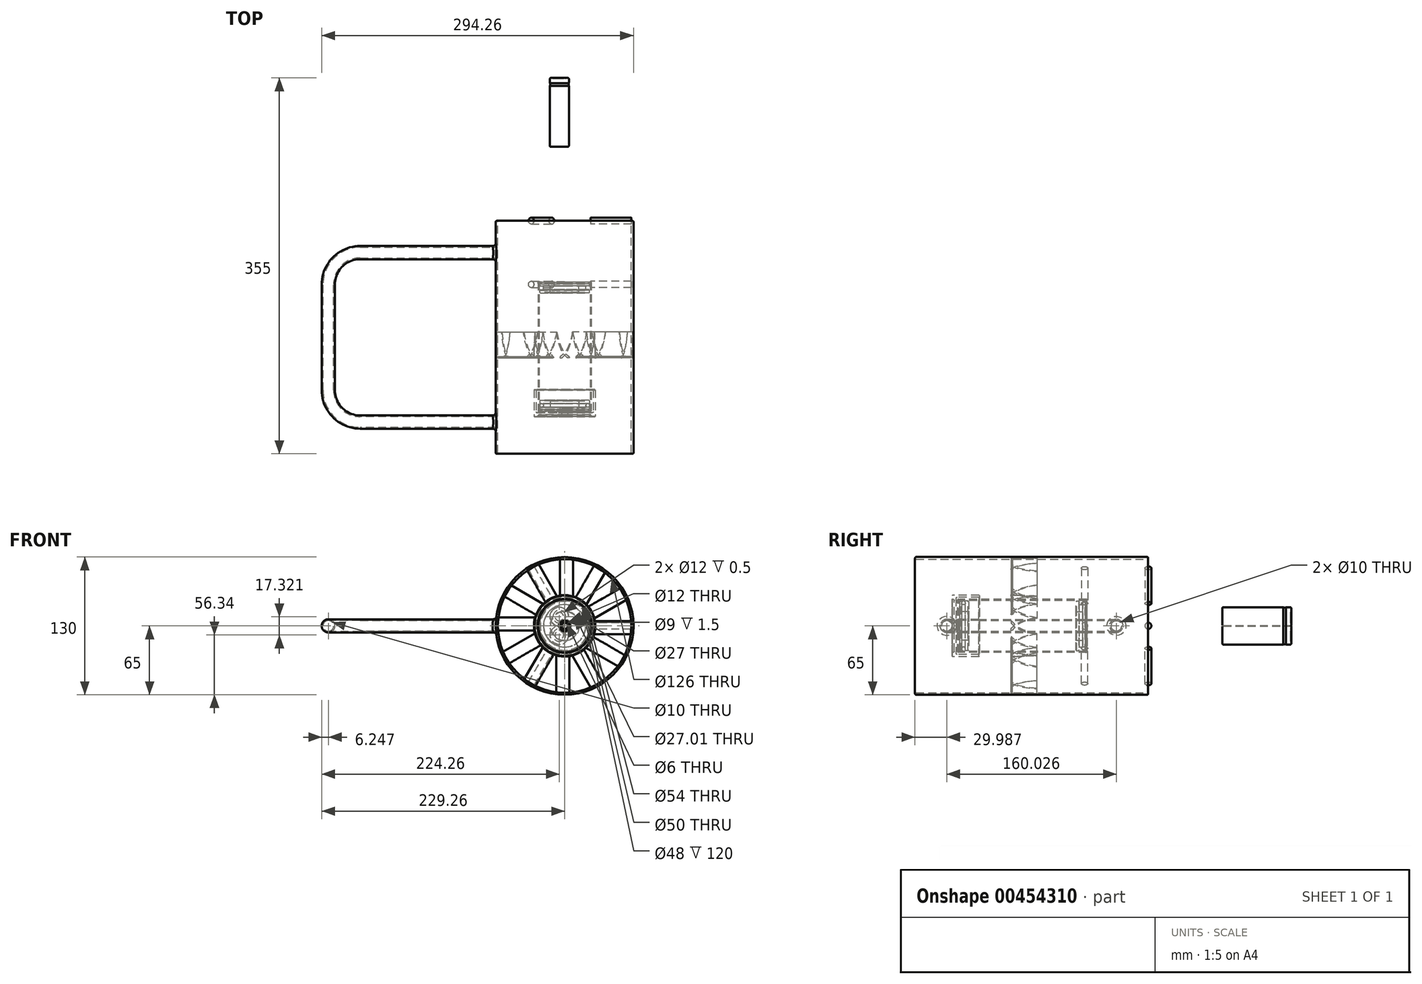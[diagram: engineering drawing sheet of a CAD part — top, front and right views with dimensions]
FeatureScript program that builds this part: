
annotation { "Feature Type Name" : "Feature", "Feature Type Description" : "" }
export const myFeature = defineFeature(function(context is Context, id is Id, definition is map)
    precondition{}
    {
        {
            var Q0;
            Q0=qCreatedBy(makeId("Right.planeOp"),FACE);
            var sketch = newSketch(context, id + "F0", { "sketchPlane" : qUnion([Q0])});
            skLineSegment(sketch, "E0", {"start": v(0, 0) * mm, "end": v(0, 5.8) * mm});
            skLineSegment(sketch, "E1", {"start": v(0.2, 6) * mm, "end": v(2, 6) * mm});
            skLineSegment(sketch, "E2", {"start": v(2, 6) * mm, "end": v(2, 4.31) * mm});
            skLineSegment(sketch, "E3", {"start": v(1.68, 3.67) * mm, "end": v(0.77, 3) * mm});
            skLineSegment(sketch, "E4", {"start": v(0.77, 3) * mm, "end": v(0.46, 3.46) * mm});
            skLineSegment(sketch, "E5", {"start": v(0.46, 3.46) * mm, "end": v(0.97, 4.13) * mm});
            skLineSegment(sketch, "E6", {"start": v(0.81, 4.53) * mm, "end": v(0, 4.66) * mm});
            skArc(sketch, "E7.filletArc", {"start": v(0.97, 4.13) * mm, "mid": v(1, 4.38) * mm, "end": v(0.81, 4.53) * mm});
            skPoint(sketch, "E8.visualSharp", {"position": v(0, 6) * mm});
            skArc(sketch, "E8.filletArc", {"start": v(0.2, 6) * mm, "mid": v(0.06, 5.94) * mm, "end": v(0, 5.8) * mm});
            skPoint(sketch, "E9.visualSharp", {"position": v(2, 3.9) * mm});
            skArc(sketch, "E9.filletArc", {"start": v(1.68, 3.67) * mm, "mid": v(1.91, 3.95) * mm, "end": v(2, 4.31) * mm});
            skLineSegment(sketch, "E10", {"start": v(-2.35, 0) * mm, "end": v(5.53, 0) * mm, "construction": true});
            skSolve(sketch);
        }
        {
            var Q0;
            Q0=qSketchRegion(id+"F0",true);
            var Q1;
            Q1=sQuery(id+"F0.wireOp",EDGE,"E10");
            revolve(context, id + "F1", {"entities" : qUnion([Q0]), "axis" : qUnion([Q1]), "revolveType" : RevolveType.FULL});
        }
        {
            var Q0;
            Q0=makeQuery(id+"F1.opRevolve","SWEPT_BODY",BODY,{"disambiguationData":[OSD([sQuery(id+"F0.wireOp",EDGE,"E0"),sQuery(id+"F0.wireOp",EDGE,"E1"),sQuery(id+"F0.wireOp",EDGE,"E2"),sQuery(id+"F0.wireOp",EDGE,"E3"),sQuery(id+"F0.wireOp",EDGE,"E4"),sQuery(id+"F0.wireOp",EDGE,"E5"),sQuery(id+"F0.wireOp",EDGE,"E6"),sQuery(id+"F0.wireOp",EDGE,"E7.filletArc"),sQuery(id+"F0.wireOp",EDGE,"E8.filletArc"),sQuery(id+"F0.wireOp",EDGE,"E9.filletArc")])]});
            var Q1;
            Q1=makeQuery(id+"F1.opRevolve","SWEPT_FACE",FACE,{"disambiguationData":[OSD([sQuery(id+"F0.wireOp",EDGE,"E1")])]});
            var Q2;
            Q2=qCreatedBy(makeId("Top.planeOp"),FACE);
            transform(context, id + "F2", {"entities" : qUnion([Q0]), "transformType" : TransformType.TRANSLATION_DISTANCE, "transformDirection" : qUnion([Q1, Q2]), "distance" : 50 * mm, "makeCopy" : false});
        }
        {
            var Q0;
            Q0=qCreatedBy(makeId("Right.planeOp"),FACE);
            var sketch = newSketch(context, id + "F3", { "sketchPlane" : qUnion([Q0])});
            skLineSegment(sketch, "E11", {"start": v(0, 0) * mm, "end": v(0, 25) * mm});
            skLineSegment(sketch, "E12", {"start": v(0, 25) * mm, "end": v(2, 25) * mm});
            skLineSegment(sketch, "E13", {"start": v(2, 25) * mm, "end": v(2, 23.5) * mm});
            skLineSegment(sketch, "E14", {"start": v(2, 23.5) * mm, "end": v(4, 23.5) * mm});
            skLineSegment(sketch, "E15", {"start": v(4, 23.5) * mm, "end": v(4, 20) * mm});
            skLineSegment(sketch, "E16", {"start": v(4, 20) * mm, "end": v(7.5, 20) * mm});
            skLineSegment(sketch, "E17", {"start": v(7.5, 20) * mm, "end": v(7.5, 23.5) * mm});
            skLineSegment(sketch, "E18", {"start": v(7.5, 23.5) * mm, "end": v(10.5, 23.5) * mm});
            skLineSegment(sketch, "E19", {"start": v(10.5, 23.5) * mm, "end": v(10.5, 13.5) * mm});
            skLineSegment(sketch, "E20", {"start": v(10.5, 13.5) * mm, "end": v(4, 13.5) * mm});
            skLineSegment(sketch, "E21", {"start": v(4, 13.5) * mm, "end": v(4, 4.5) * mm});
            skLineSegment(sketch, "E22", {"start": v(4, 4.5) * mm, "end": v(2.5, 4.5) * mm});
            skLineSegment(sketch, "E23", {"start": v(2.5, 4.5) * mm, "end": v(2.5, 6) * mm});
            skLineSegment(sketch, "E24", {"start": v(2.5, 6) * mm, "end": v(0, 6) * mm});
            skLineSegment(sketch, "E25", {"start": v(-5.31, 0) * mm, "end": v(25.38, 0) * mm, "construction": true});
            skSolve(sketch);
        }
        {
            var Q0;
            Q0=qSketchRegion(id+"F3",true);
            var Q1;
            Q1=sQuery(id+"F3.wireOp",EDGE,"E25");
            revolve(context, id + "F4", {"entities" : qUnion([Q0]), "axis" : qUnion([Q1]), "revolveType" : RevolveType.FULL});
        }
        {
            var Q0;
            Q0=makeQuery(id+"F4.opRevolve","SWEPT_EDGE",EDGE,{"disambiguationData":[OSD([sQuery(id+"F3.wireOp",EDGE,"E11"),sQuery(id+"F3.wireOp",EDGE,"E24")])]});
            chamfer(context, id + "F5", {"entities" : qUnion([Q0]), "chamferType" : ChamferType.OFFSET_ANGLE, "width" : .5 * mm, "oppositeDirection" : false, "angle" : 30 * degree, "tangentPropagation" : true});
        }
        {
            var Q0;
            Q0=makeQuery(id+"F4.opRevolve","SWEPT_EDGE",EDGE,{"disambiguationData":[OSD([sQuery(id+"F3.wireOp",EDGE,"E23"),sQuery(id+"F3.wireOp",EDGE,"E24")])]});
            var Q1;
            Q1=makeQuery(id+"F4.opRevolve","SWEPT_EDGE",EDGE,{"disambiguationData":[OSD([sQuery(id+"F3.wireOp",EDGE,"E17"),sQuery(id+"F3.wireOp",EDGE,"E18")])]});
            var Q2;
            Q2=makeQuery(id+"F4.opRevolve","SWEPT_EDGE",EDGE,{"disambiguationData":[OSD([sQuery(id+"F3.wireOp",EDGE,"E15"),sQuery(id+"F3.wireOp",EDGE,"E16")])]});
            var Q3;
            Q3=makeQuery(id+"F4.opRevolve","SWEPT_EDGE",EDGE,{"disambiguationData":[OSD([sQuery(id+"F3.wireOp",EDGE,"E20"),sQuery(id+"F3.wireOp",EDGE,"E21")])]});
            fillet(context, id + "F6", {"entities" : qUnion([Q0, Q1, Q2, Q3]), "radius" : .3 * mm, "tangentPropagation" : true, "allowEdgeOverflow" : false});
        }
        {
            var Q0;
            Q0=makeQuery(id+"F4.opRevolve","SWEPT_EDGE",EDGE,{"disambiguationData":[OSD([sQuery(id+"F3.wireOp",EDGE,"E11"),sQuery(id+"F3.wireOp",EDGE,"E12")])]});
            var Q1;
            Q1=makeQuery(id+"F4.opRevolve","SWEPT_EDGE",EDGE,{"disambiguationData":[OSD([sQuery(id+"F3.wireOp",EDGE,"E12"),sQuery(id+"F3.wireOp",EDGE,"E13")])]});
            var Q2;
            Q2=makeQuery(id+"F4.opRevolve","SWEPT_EDGE",EDGE,{"disambiguationData":[OSD([sQuery(id+"F3.wireOp",EDGE,"E14"),sQuery(id+"F3.wireOp",EDGE,"E15")])]});
            var Q3;
            Q3=makeQuery(id+"F4.opRevolve","SWEPT_EDGE",EDGE,{"disambiguationData":[OSD([sQuery(id+"F3.wireOp",EDGE,"E17"),sQuery(id+"F3.wireOp",EDGE,"E18")])]});
            var Q4;
            Q4=makeQuery(id+"F4.opRevolve","SWEPT_EDGE",EDGE,{"disambiguationData":[OSD([sQuery(id+"F3.wireOp",EDGE,"E18"),sQuery(id+"F3.wireOp",EDGE,"E19")])]});
            var Q5;
            Q5=makeQuery(id+"F4.opRevolve","SWEPT_EDGE",EDGE,{"disambiguationData":[OSD([sQuery(id+"F3.wireOp",EDGE,"E19"),sQuery(id+"F3.wireOp",EDGE,"E20")])]});
            chamfer(context, id + "F7", {"entities" : qUnion([Q0, Q1, Q2, Q3, Q4, Q5]), "width" : .5 * mm, "tangentPropagation" : true});
        }
        {
            var Q0;
            Q0=qCreatedBy(makeId("Right.planeOp"),FACE);
            var sketch = newSketch(context, id + "F8", { "sketchPlane" : qUnion([Q0])});
            skCircle(sketch, "E26", {"center": v(5.75, 21.75) * mm, "radius": 1.75 * mm});
            skLineSegment(sketch, "E27", {"start": v(-6.06, 0) * mm, "end": v(25.96, 0) * mm, "construction": true});
            skSolve(sketch);
        }
        {
            var Q0;
            Q0=makeQuery(id+"F8.imprint","IMPRINT",FACE,{"disambiguationData":[TD([[makeQuery(id+"F8.imprint","IMPRINT",EDGE,{"derivedFrom":sQuery(id+"F8.wireOp",EDGE,"E26")}),1.0]])]});
            var Q1;
            Q1=sQuery(id+"F8.wireOp",EDGE,"E27");
            revolve(context, id + "F9", {"operationType" : NewBodyOperationType.ADD, "entities" : qUnion([Q0]), "axis" : qUnion([Q1]), "revolveType" : RevolveType.FULL});
        }
        {
            var Q0;
            Q0=makeQuery(id+"F4.opRevolve","SWEPT_BODY",BODY,{"disambiguationData":[OSD([sQuery(id+"F3.wireOp",EDGE,"E11"),sQuery(id+"F3.wireOp",EDGE,"E12"),sQuery(id+"F3.wireOp",EDGE,"E13"),sQuery(id+"F3.wireOp",EDGE,"E14"),sQuery(id+"F3.wireOp",EDGE,"E15"),sQuery(id+"F3.wireOp",EDGE,"E16"),sQuery(id+"F3.wireOp",EDGE,"E17"),sQuery(id+"F3.wireOp",EDGE,"E18"),sQuery(id+"F3.wireOp",EDGE,"E19"),sQuery(id+"F3.wireOp",EDGE,"E20"),sQuery(id+"F3.wireOp",EDGE,"E21"),sQuery(id+"F3.wireOp",EDGE,"E22"),sQuery(id+"F3.wireOp",EDGE,"E23"),sQuery(id+"F3.wireOp",EDGE,"E24")])]});
            var Q1;
            Q1=makeQuery(id+"F9.opRevolve","SWEPT_BODY",BODY,{"disambiguationData":[OSD([sQuery(id+"F8.wireOp",EDGE,"E26")])]});
            var Q2;
            Q2=makeQuery(id+"F4.opRevolve","SWEPT_FACE",FACE,{"disambiguationData":[OSD([sQuery(id+"F3.wireOp",EDGE,"E18")])]});
            transform(context, id + "F10", {"entities" : qUnion([Q0, Q1]), "transformType" : TransformType.TRANSLATION_DISTANCE, "transformDirection" : qUnion([Q2]), "distance" : 50 * mm, "makeCopy" : false});
        }
        {
            var Q0;
            Q0=qCreatedBy(makeId("Right.planeOp"),FACE);
            var sketch = newSketch(context, id + "F11", { "sketchPlane" : qUnion([Q0])});
            skLineSegment(sketch, "E28", {"start": v(0, 3) * mm, "end": v(0, 5) * mm});
            skLineSegment(sketch, "E29", {"start": v(0, 5) * mm, "end": v(2, 5) * mm});
            skLineSegment(sketch, "E30", {"start": v(2, 5) * mm, "end": v(2, 25) * mm});
            skLineSegment(sketch, "E31", {"start": v(2, 25) * mm, "end": v(0, 25) * mm});
            skLineSegment(sketch, "E32", {"start": v(0, 25) * mm, "end": v(0, 29) * mm});
            skLineSegment(sketch, "E33", {"start": v(0, 29) * mm, "end": v(25.72, 29) * mm});
            skLineSegment(sketch, "E34", {"start": v(25.72, 29) * mm, "end": v(25.72, 27) * mm});
            skLineSegment(sketch, "E35", {"start": v(25.72, 27) * mm, "end": v(3.72, 27) * mm});
            skLineSegment(sketch, "E36", {"start": v(3.72, 27) * mm, "end": v(3.72, 5) * mm});
            skLineSegment(sketch, "E37", {"start": v(3.72, 5) * mm, "end": v(5.72, 5) * mm});
            skLineSegment(sketch, "E38", {"start": v(5.72, 5) * mm, "end": v(5.72, 3) * mm});
            skLineSegment(sketch, "E39", {"start": v(5.72, 3) * mm, "end": v(0, 3) * mm});
            skLineSegment(sketch, "E40", {"start": v(-6.87, 0) * mm, "end": v(43.92, 0) * mm, "construction": true});
            skSolve(sketch);
        }
        {
            var Q0;
            Q0=qSketchRegion(id+"F11",true);
            var Q1;
            Q1=sQuery(id+"F11.wireOp",EDGE,"E40");
            revolve(context, id + "F12", {"entities" : qUnion([Q0]), "axis" : qUnion([Q1]), "revolveType" : RevolveType.FULL});
        }
        {
            var Q0;
            Q0=makeQuery(id+"F12.opRevolve","SWEPT_EDGE",EDGE,{"disambiguationData":[OSD([sQuery(id+"F11.wireOp",EDGE,"E28"),sQuery(id+"F11.wireOp",EDGE,"E39")])]});
            var Q1;
            Q1=makeQuery(id+"F12.opRevolve","SWEPT_EDGE",EDGE,{"disambiguationData":[OSD([sQuery(id+"F11.wireOp",EDGE,"E28"),sQuery(id+"F11.wireOp",EDGE,"E29")])]});
            var Q2;
            Q2=makeQuery(id+"F12.opRevolve","SWEPT_EDGE",EDGE,{"disambiguationData":[OSD([sQuery(id+"F11.wireOp",EDGE,"E31"),sQuery(id+"F11.wireOp",EDGE,"E32")])]});
            var Q3;
            Q3=makeQuery(id+"F12.opRevolve","SWEPT_EDGE",EDGE,{"disambiguationData":[OSD([sQuery(id+"F11.wireOp",EDGE,"E32"),sQuery(id+"F11.wireOp",EDGE,"E33")])]});
            var Q4;
            Q4=makeQuery(id+"F12.opRevolve","SWEPT_EDGE",EDGE,{"disambiguationData":[OSD([sQuery(id+"F11.wireOp",EDGE,"E33"),sQuery(id+"F11.wireOp",EDGE,"E34")])]});
            var Q5;
            Q5=makeQuery(id+"F12.opRevolve","SWEPT_EDGE",EDGE,{"disambiguationData":[OSD([sQuery(id+"F11.wireOp",EDGE,"E34"),sQuery(id+"F11.wireOp",EDGE,"E35")])]});
            var Q6;
            Q6=makeQuery(id+"F12.opRevolve","SWEPT_EDGE",EDGE,{"disambiguationData":[OSD([sQuery(id+"F11.wireOp",EDGE,"E37"),sQuery(id+"F11.wireOp",EDGE,"E38")])]});
            var Q7;
            Q7=makeQuery(id+"F12.opRevolve","SWEPT_EDGE",EDGE,{"disambiguationData":[OSD([sQuery(id+"F11.wireOp",EDGE,"E38"),sQuery(id+"F11.wireOp",EDGE,"E39")])]});
            chamfer(context, id + "F13", {"entities" : qUnion([Q0, Q1, Q2, Q3, Q4, Q5, Q6, Q7]), "width" : .5 * mm, "tangentPropagation" : true});
        }
        {
            var Q0;
            Q0=makeQuery(id+"F12.opRevolve","SWEPT_EDGE",EDGE,{"disambiguationData":[OSD([sQuery(id+"F11.wireOp",EDGE,"E29"),sQuery(id+"F11.wireOp",EDGE,"E30")])]});
            var Q1;
            Q1=makeQuery(id+"F12.opRevolve","SWEPT_EDGE",EDGE,{"disambiguationData":[OSD([sQuery(id+"F11.wireOp",EDGE,"E30"),sQuery(id+"F11.wireOp",EDGE,"E31")])]});
            var Q2;
            Q2=makeQuery(id+"F12.opRevolve","SWEPT_EDGE",EDGE,{"disambiguationData":[OSD([sQuery(id+"F11.wireOp",EDGE,"E35"),sQuery(id+"F11.wireOp",EDGE,"E36")])]});
            var Q3;
            Q3=makeQuery(id+"F12.opRevolve","SWEPT_EDGE",EDGE,{"disambiguationData":[OSD([sQuery(id+"F11.wireOp",EDGE,"E36"),sQuery(id+"F11.wireOp",EDGE,"E37")])]});
            fillet(context, id + "F14", {"entities" : qUnion([Q0, Q1, Q2, Q3]), "radius" : 1 * mm, "tangentPropagation" : true, "allowEdgeOverflow" : false});
        }
        {
            var Q0;
            Q0=qCreatedBy(makeId("Right.planeOp"),FACE);
            cPlane(context, id + "F15", {"entities" : qUnion([Q0]), "cplaneType" : CPlaneType.OFFSET, "offset" : 29 * mm, "width" : 150 * mm, "height" : 150 * mm});
        }
        {
            var Q0;
            Q0=qCreatedBy(id+"F15.planeOp",FACE);
            var sketch = newSketch(context, id + "F16", { "sketchPlane" : qUnion([Q0])});
            skFitSpline(sketch, "E41", {"points": [v(1.8, 4) * mm, v(0.76, 4.47) * mm, v(0.51, 3.63) * mm, v(0.79, 2.55) * mm, v(4.93, -1.3) * mm, v(11.9, -4.72) * mm, v(18.63, -6.73) * mm, v(25, -7.85) * mm], "startDerivative": vector(-10.22, 8.26) * mm, "endDerivative": vector(8.4, -0.71) * mm});
            skFitSpline(sketch, "E42", {"points": [v(25, -7.85) * mm, v(25.14, -7.8) * mm, v(24.7, -7.38) * mm, v(23.01, -6.96) * mm, v(19.16, -6.12) * mm, v(12.02, -3.74) * mm, v(5.67, -0.3) * mm, v(3.11, 2.55) * mm, v(1.8, 4) * mm], "startDerivative": vector(9.33, 0.6) * mm, "endDerivative": vector(-14.15, 14.4) * mm});
            skSolve(sketch);
        }
        {
            var Q0;
            Q0=qSketchRegion(id+"F16",true);
            extrude(context, id + "F17", {"entities" : qUnion([Q0]), "depth" : 35 * mm, "hasSecondDirection" : true, "secondDirectionOppositeDirection" : true, "secondDirectionDepth" : 1.6 * mm});
        }
        {
            var Q0;
            Q0=makeQuery(id+"F12.opRevolve","SWEPT_BODY",BODY,{"disambiguationData":[OSD([sQuery(id+"F11.wireOp",EDGE,"E28"),sQuery(id+"F11.wireOp",EDGE,"E29"),sQuery(id+"F11.wireOp",EDGE,"E30"),sQuery(id+"F11.wireOp",EDGE,"E31"),sQuery(id+"F11.wireOp",EDGE,"E32"),sQuery(id+"F11.wireOp",EDGE,"E33"),sQuery(id+"F11.wireOp",EDGE,"E34"),sQuery(id+"F11.wireOp",EDGE,"E35"),sQuery(id+"F11.wireOp",EDGE,"E36"),sQuery(id+"F11.wireOp",EDGE,"E37"),sQuery(id+"F11.wireOp",EDGE,"E38"),sQuery(id+"F11.wireOp",EDGE,"E39")])]});
            var Q1;
            Q1=makeQuery(id+"F17.opExtrude","SWEPT_BODY",BODY,{"disambiguationData":[OSD([sQuery(id+"F16.wireOp",EDGE,"E41"),sQuery(id+"F16.wireOp",EDGE,"E42")])]});
            booleanBodies(context, id + "F18", {"operationType" : BooleanOperationType.SUBTRACTION, "tools" : qUnion([Q0]), "targets" : qUnion([Q1]), "keepTools" : true});
        }
        {
            var Q0;
            Q0=makeQuery(id+"F17.opExtrude","SWEPT_BODY",BODY,{"disambiguationData":[OSD([sQuery(id+"F16.wireOp",EDGE,"E41"),sQuery(id+"F16.wireOp",EDGE,"E42")])]});
            var Q1;
            Q1=makeQuery(id+"F12.opRevolve","SWEPT_FACE",FACE,{"disambiguationData":[OSD([sQuery(id+"F11.wireOp",EDGE,"E33")])]});
            circularPattern(context, id + "F19", {"entities" : qUnion([Q0]), "axis" : qUnion([Q1]), "angle" : 360 * degree, "instanceCount" : 12, "equalSpace" : true});
        }
        {
            var Q0;
            Q0=makeQuery(id+"F12.opRevolve","SWEPT_BODY",BODY,{"disambiguationData":[OSD([sQuery(id+"F11.wireOp",EDGE,"E28"),sQuery(id+"F11.wireOp",EDGE,"E29"),sQuery(id+"F11.wireOp",EDGE,"E30"),sQuery(id+"F11.wireOp",EDGE,"E31"),sQuery(id+"F11.wireOp",EDGE,"E32"),sQuery(id+"F11.wireOp",EDGE,"E33"),sQuery(id+"F11.wireOp",EDGE,"E34"),sQuery(id+"F11.wireOp",EDGE,"E35"),sQuery(id+"F11.wireOp",EDGE,"E36"),sQuery(id+"F11.wireOp",EDGE,"E37"),sQuery(id+"F11.wireOp",EDGE,"E38"),sQuery(id+"F11.wireOp",EDGE,"E39")])]});
            var Q1;
            Q1=makeQuery(id+"F4.opRevolve","SWEPT_FACE",FACE,{"disambiguationData":[OSD([sQuery(id+"F3.wireOp",EDGE,"E18")])]});
            transform(context, id + "F20", {"entities" : qUnion([Q0]), "transformType" : TransformType.TRANSLATION_DISTANCE, "transformDirection" : qUnion([Q1]), "distance" : 120 * mm, "makeCopy" : false});
        }
        {
            var Q0;
            Q0=qCreatedBy(makeId("Front.planeOp"),FACE);
            var sketch = newSketch(context, id + "F21", { "sketchPlane" : qUnion([Q0])});
            skCircle(sketch, "E43", {"center": v(0, 0) * mm, "radius": 65 * mm});
            skCircle(sketch, "E44", {"center": v(0, 0) * mm, "radius": 63 * mm});
            skSolve(sketch);
        }
        {
            var Q0;
            Q0=qSketchRegion(id+"F21",true);
            extrude(context, id + "F22", {"entities" : qUnion([Q0]), "depth" : 220 * mm});
        }
        {
            var Q0;
            Q0=makeQuery(id+"F22.opExtrude","CAP_EDGE",EDGE,{"disambiguationData":[OSD([sQuery(id+"F21.wireOp",EDGE,"E43")])],"isStart":false});
            var Q1;
            Q1=makeQuery(id+"F22.opExtrude","CAP_EDGE",EDGE,{"disambiguationData":[OSD([sQuery(id+"F21.wireOp",EDGE,"E44")])],"isStart":false});
            var Q2;
            Q2=makeQuery(id+"F22.opExtrude","CAP_EDGE",EDGE,{"disambiguationData":[OSD([sQuery(id+"F21.wireOp",EDGE,"E43")])],"isStart":true});
            var Q3;
            Q3=makeQuery(id+"F22.opExtrude","CAP_EDGE",EDGE,{"disambiguationData":[OSD([sQuery(id+"F21.wireOp",EDGE,"E44")])],"isStart":true});
            fillet(context, id + "F23", {"entities" : qUnion([Q0, Q1, Q2, Q3]), "radius" : 1 * mm, "tangentPropagation" : true, "allowEdgeOverflow" : false});
        }
        {
            var Q0;
            Q0=makeQuery(id+"F22.opExtrude","SWEPT_BODY",BODY,{"disambiguationData":[OSD([sQuery(id+"F21.wireOp",EDGE,"E43"),sQuery(id+"F21.wireOp",EDGE,"E44")])]});
            var Q1;
            Q1=makeQuery(id+"F12.opRevolve","SWEPT_BODY",BODY,{"disambiguationData":[OSD([sQuery(id+"F11.wireOp",EDGE,"E28"),sQuery(id+"F11.wireOp",EDGE,"E29"),sQuery(id+"F11.wireOp",EDGE,"E30"),sQuery(id+"F11.wireOp",EDGE,"E31"),sQuery(id+"F11.wireOp",EDGE,"E32"),sQuery(id+"F11.wireOp",EDGE,"E33"),sQuery(id+"F11.wireOp",EDGE,"E34"),sQuery(id+"F11.wireOp",EDGE,"E35"),sQuery(id+"F11.wireOp",EDGE,"E36"),sQuery(id+"F11.wireOp",EDGE,"E37"),sQuery(id+"F11.wireOp",EDGE,"E38"),sQuery(id+"F11.wireOp",EDGE,"E39")])]});
            booleanBodies(context, id + "F24", {"operationType" : BooleanOperationType.SUBTRACTION, "tools" : qUnion([Q0]), "targets" : qUnion([Q1]), "keepTools" : true});
        }
        {
            var Q0;
            Q0=makeQuery(id+"F22.opExtrude","SWEPT_BODY",BODY,{"disambiguationData":[OSD([sQuery(id+"F21.wireOp",EDGE,"E43"),sQuery(id+"F21.wireOp",EDGE,"E44")])]});
            var Q1;
            Q1=makeQuery(id+"F22.opExtrude","SWEPT_FACE",FACE,{"disambiguationData":[OSD([sQuery(id+"F21.wireOp",EDGE,"E43")])]});
            transform(context, id + "F25", {"entities" : qUnion([Q0]), "transformType" : TransformType.TRANSLATION_DISTANCE, "transformDirection" : qUnion([Q1]), "distance" : 200 * mm, "oppositeDirection" : true, "makeCopy" : false});
        }
        {
            var Q0;
            Q0=qCreatedBy(makeId("Front.planeOp"),FACE);
            var sketch = newSketch(context, id + "F26", { "sketchPlane" : qUnion([Q0])});
            skCircle(sketch, "E45", {"center": v(0, 0) * mm, "radius": 25 * mm});
            skCircle(sketch, "E46", {"center": v(0, 0) * mm, "radius": 24 * mm});
            skSolve(sketch);
        }
        {
            var Q0;
            Q0=qSketchRegion(id+"F26",true);
            extrude(context, id + "F27", {"entities" : qUnion([Q0]), "oppositeDirection" : true, "depth" : 120 * mm});
        }
        {
            var Q0;
            Q0=makeQuery(id+"F27.opExtrude","SWEPT_BODY",BODY,{"disambiguationData":[OSD([sQuery(id+"F26.wireOp",EDGE,"E45"),sQuery(id+"F26.wireOp",EDGE,"E46")])]});
            var Q1;
            Q1=makeQuery(id+"F27.opExtrude","SWEPT_FACE",FACE,{"disambiguationData":[OSD([sQuery(id+"F26.wireOp",EDGE,"E45")])]});
            transform(context, id + "F28", {"entities" : qUnion([Q0]), "transformType" : TransformType.TRANSLATION_DISTANCE, "transformDirection" : qUnion([Q1]), "distance" : 25 * mm, "oppositeDirection" : true, "makeCopy" : false});
        }
        {
            var Q0;
            Q0=qCreatedBy(id+"F15.planeOp",FACE);
            var sketch = newSketch(context, id + "F29", { "sketchPlane" : qUnion([Q0])});
            skCircle(sketch, "E47", {"center": v(0, 0) * mm, "radius": 3 * mm});
            skCircle(sketch, "E48", {"center": v(60, 0) * mm, "radius": 3 * mm});
            skSolve(sketch);
        }
        {
            var Q0;
            Q0=qSketchRegion(id+"F29",true);
            extrude(context, id + "F30", {"entities" : qUnion([Q0]), "depth" : 34 * mm, "hasSecondDirection" : true, "secondDirectionOppositeDirection" : true, "secondDirectionDepth" : 4.5 * mm});
        }
        {
            var Q0;
            Q0=makeQuery(id+"F30.opExtrude","SWEPT_BODY",BODY,{"disambiguationData":[OSD([sQuery(id+"F29.wireOp",EDGE,"E47")])]});
            var Q1;
            Q1=makeQuery(id+"F30.opExtrude","SWEPT_BODY",BODY,{"disambiguationData":[OSD([sQuery(id+"F29.wireOp",EDGE,"E48")])]});
            var Q2;
            Q2=makeQuery(id+"F27.opExtrude","SWEPT_FACE",FACE,{"disambiguationData":[OSD([sQuery(id+"F26.wireOp",EDGE,"E45")])]});
            transform(context, id + "F31", {"entities" : qUnion([Q0, Q1]), "transformType" : TransformType.TRANSLATION_DISTANCE, "transformDirection" : qUnion([Q2]), "distance" : 70 * mm, "oppositeDirection" : true, "makeCopy" : false});
        }
        {
            var Q0;
            Q0=makeQuery(id+"F30.opExtrude","SWEPT_BODY",BODY,{"disambiguationData":[OSD([sQuery(id+"F29.wireOp",EDGE,"E47")])]});
            var Q1;
            Q1=makeQuery(id+"F30.opExtrude","SWEPT_BODY",BODY,{"disambiguationData":[OSD([sQuery(id+"F29.wireOp",EDGE,"E48")])]});
            var Q2;
            Q2=makeQuery(id+"F27.opExtrude","SWEPT_FACE",FACE,{"disambiguationData":[OSD([sQuery(id+"F26.wireOp",EDGE,"E45")])]});
            circularPattern(context, id + "F32", {"entities" : qUnion([Q0, Q1]), "axis" : qUnion([Q2]), "angle" : 360 * degree, "instanceCount" : 3, "equalSpace" : true});
        }
        {
            var Q0;
            Q0=makeQuery(id+"F27.opExtrude","SWEPT_BODY",BODY,{"disambiguationData":[OSD([sQuery(id+"F26.wireOp",EDGE,"E45"),sQuery(id+"F26.wireOp",EDGE,"E46")])]});
            var Q1;
            Q1=makeQuery(id+"F27.opExtrude","SWEPT_FACE",FACE,{"disambiguationData":[OSD([sQuery(id+"F26.wireOp",EDGE,"E45")])]});
            transform(context, id + "F33", {"entities" : qUnion([Q0]), "transformType" : TransformType.ROTATION, "transformAxis" : qUnion([Q1]), "angle" : 30 * degree, "oppositeDirection" : true, "makeCopy" : false});
        }
        {
            var Q0;
            Q0=qCreatedBy(makeId("Right.planeOp"),FACE);
            var sketch = newSketch(context, id + "F34", { "sketchPlane" : qUnion([Q0])});
            skLineSegment(sketch, "E49", {"start": v(0, 0) * mm, "end": v(30.7, 0) * mm, "construction": true});
            skLineSegment(sketch, "E50.MirrorCS", {"start": v(-16.1, 23.5) * mm, "end": v(-16.1, 13.5) * mm});
            skLineSegment(sketch, "E51.MirrorCS", {"start": v(-13.1, 23.5) * mm, "end": v(-16.1, 23.5) * mm});
            skLineSegment(sketch, "E52.MirrorCS", {"start": v(-13.1, 20) * mm, "end": v(-13.1, 23.5) * mm});
            skLineSegment(sketch, "E53.MirrorCS", {"start": v(-9.6, 13.5) * mm, "end": v(-9.6, 0) * mm});
            skLineSegment(sketch, "E54.MirrorCS", {"start": v(-9.6, 20) * mm, "end": v(-13.1, 20) * mm});
            skLineSegment(sketch, "E55.MirrorCS", {"start": v(-9.6, 23.5) * mm, "end": v(-9.6, 20) * mm});
            skLineSegment(sketch, "E56.MirrorCS", {"start": v(-7.6, 23.5) * mm, "end": v(-9.6, 23.5) * mm});
            skLineSegment(sketch, "E57.MirrorCS", {"start": v(-7.6, 25) * mm, "end": v(-7.6, 23.5) * mm});
            skLineSegment(sketch, "E58.MirrorCS", {"start": v(-5.6, 25) * mm, "end": v(-7.6, 25) * mm});
            skLineSegment(sketch, "E59.MirrorCS", {"start": v(-5.68, 0) * mm, "end": v(-5.6, 25) * mm});
            skLineSegment(sketch, "E60.MirrorCS", {"start": v(-16.1, 13.5) * mm, "end": v(-9.6, 13.5) * mm});
            skLineSegment(sketch, "E61.MirrorCS", {"start": v(-9.6, 0) * mm, "end": v(-5.68, 0) * mm});
            skSolve(sketch);
        }
        {
            var Q0;
            Q0=qSketchRegion(id+"F34",true);
            var Q1;
            Q1=makeQuery(id+"F27.opExtrude","SWEPT_FACE",FACE,{"disambiguationData":[OSD([sQuery(id+"F26.wireOp",EDGE,"E45")])]});
            revolve(context, id + "F35", {"entities" : qUnion([Q0]), "axis" : qUnion([Q1]), "revolveType" : RevolveType.FULL});
        }
        {
            var Q0;
            Q0=makeQuery(id+"F35.opRevolve","SWEPT_BODY",BODY,{"disambiguationData":[OSD([sQuery(id+"F34.wireOp",EDGE,"E50.MirrorCS"),sQuery(id+"F34.wireOp",EDGE,"E51.MirrorCS"),sQuery(id+"F34.wireOp",EDGE,"E52.MirrorCS"),sQuery(id+"F34.wireOp",EDGE,"E53.MirrorCS"),sQuery(id+"F34.wireOp",EDGE,"E54.MirrorCS"),sQuery(id+"F34.wireOp",EDGE,"E55.MirrorCS"),sQuery(id+"F34.wireOp",EDGE,"E56.MirrorCS"),sQuery(id+"F34.wireOp",EDGE,"E57.MirrorCS"),sQuery(id+"F34.wireOp",EDGE,"E58.MirrorCS"),sQuery(id+"F34.wireOp",EDGE,"E59.MirrorCS"),sQuery(id+"F34.wireOp",EDGE,"E60.MirrorCS"),sQuery(id+"F34.wireOp",EDGE,"E61.MirrorCS")])]});
            var Q1;
            Q1=makeQuery(id+"F27.opExtrude","SWEPT_FACE",FACE,{"disambiguationData":[OSD([sQuery(id+"F26.wireOp",EDGE,"E45")])]});
            transform(context, id + "F36", {"entities" : qUnion([Q0]), "transformType" : TransformType.TRANSLATION_DISTANCE, "transformDirection" : qUnion([Q1]), "distance" : 78 * mm, "oppositeDirection" : true, "makeCopy" : false});
        }
        {
            var Q0;
            Q0=makeQuery(id+"F35.opRevolve","SWEPT_EDGE",EDGE,{"disambiguationData":[OSD([sQuery(id+"F34.wireOp",EDGE,"E50.MirrorCS"),sQuery(id+"F34.wireOp",EDGE,"E51.MirrorCS")])]});
            var Q1;
            Q1=makeQuery(id+"F35.opRevolve","SWEPT_EDGE",EDGE,{"disambiguationData":[OSD([sQuery(id+"F34.wireOp",EDGE,"E51.MirrorCS"),sQuery(id+"F34.wireOp",EDGE,"E52.MirrorCS")])]});
            var Q2;
            Q2=makeQuery(id+"F35.opRevolve","SWEPT_EDGE",EDGE,{"disambiguationData":[OSD([sQuery(id+"F34.wireOp",EDGE,"E57.MirrorCS"),sQuery(id+"F34.wireOp",EDGE,"E58.MirrorCS")])]});
            var Q3;
            Q3=makeQuery(id+"F35.opRevolve","SWEPT_EDGE",EDGE,{"disambiguationData":[OSD([sQuery(id+"F34.wireOp",EDGE,"E58.MirrorCS"),sQuery(id+"F34.wireOp",EDGE,"E59.MirrorCS")])]});
            var Q4;
            Q4=makeQuery(id+"F35.opRevolve","SWEPT_EDGE",EDGE,{"disambiguationData":[OSD([sQuery(id+"F34.wireOp",EDGE,"E50.MirrorCS"),sQuery(id+"F34.wireOp",EDGE,"E60.MirrorCS")])]});
            chamfer(context, id + "F37", {"entities" : qUnion([Q0, Q1, Q2, Q3, Q4]), "width" : .5 * mm, "tangentPropagation" : true});
        }
        {
            var Q0;
            Q0=makeQuery(id+"F35.opRevolve","SWEPT_EDGE",EDGE,{"disambiguationData":[OSD([sQuery(id+"F34.wireOp",EDGE,"E53.MirrorCS"),sQuery(id+"F34.wireOp",EDGE,"E60.MirrorCS")])]});
            var Q1;
            Q1=makeQuery(id+"F35.opRevolve","SWEPT_EDGE",EDGE,{"disambiguationData":[OSD([sQuery(id+"F34.wireOp",EDGE,"E54.MirrorCS"),sQuery(id+"F34.wireOp",EDGE,"E55.MirrorCS")])]});
            var Q2;
            Q2=makeQuery(id+"F35.opRevolve","SWEPT_EDGE",EDGE,{"disambiguationData":[OSD([sQuery(id+"F34.wireOp",EDGE,"E52.MirrorCS"),sQuery(id+"F34.wireOp",EDGE,"E54.MirrorCS")])]});
            fillet(context, id + "F38", {"entities" : qUnion([Q0, Q1, Q2]), "radius" : .5 * mm, "tangentPropagation" : true, "allowEdgeOverflow" : false});
        }
        {
            var Q0;
            Q0=makeQuery(id+"F9.opRevolve","SWEPT_BODY",BODY,{"disambiguationData":[OSD([sQuery(id+"F8.wireOp",EDGE,"E26")])]});
            var Q1;
            Q1=makeQuery(id+"F27.opExtrude","SWEPT_FACE",FACE,{"disambiguationData":[OSD([sQuery(id+"F26.wireOp",EDGE,"E45")])]});
            transform(context, id + "F39", {"entities" : qUnion([Q0]), "transformType" : TransformType.TRANSLATION_DISTANCE, "transformDirection" : qUnion([Q1]), "distance" : 157.9 * mm, "oppositeDirection" : true, "makeCopy" : true});
        }
        {
            var Q0;
            Q0=qCreatedBy(makeId("Right.planeOp"),FACE);
            var sketch = newSketch(context, id + "F40", { "sketchPlane" : qUnion([Q0])});
            skLineSegment(sketch, "E62", {"start": v(0, 0) * mm, "end": v(0, 9) * mm});
            skLineSegment(sketch, "E63", {"start": v(0, 9) * mm, "end": v(57.5, 9) * mm});
            skLineSegment(sketch, "E64", {"start": v(57.5, 9) * mm, "end": v(57.5, 8.7) * mm});
            skLineSegment(sketch, "E65", {"start": v(57.5, 8.7) * mm, "end": v(60, 8.7) * mm});
            skLineSegment(sketch, "E66", {"start": v(60, 8.7) * mm, "end": v(60, 9) * mm});
            skLineSegment(sketch, "E67", {"start": v(60, 9) * mm, "end": v(65, 9) * mm});
            skLineSegment(sketch, "E68", {"start": v(65, 0) * mm, "end": v(0, 0) * mm});
            skLineSegment(sketch, "E69", {"start": v(65, 9) * mm, "end": v(65, 6) * mm});
            skLineSegment(sketch, "E70", {"start": v(65, 6) * mm, "end": v(64.5, 6) * mm});
            skLineSegment(sketch, "E71", {"start": v(64.5, 6) * mm, "end": v(64.5, 4) * mm});
            skLineSegment(sketch, "E72", {"start": v(64.5, 4) * mm, "end": v(65, 4) * mm});
            skLineSegment(sketch, "E73", {"start": v(65, 4) * mm, "end": v(65, 0) * mm});
            skSolve(sketch);
        }
        {
            var Q0;
            Q0=qSketchRegion(id+"F40",true);
            var Q1;
            Q1=makeQuery(id+"F4.opRevolve","SWEPT_FACE",FACE,{"disambiguationData":[OSD([sQuery(id+"F3.wireOp",EDGE,"E18")])]});
            revolve(context, id + "F41", {"entities" : qUnion([Q0]), "axis" : qUnion([Q1]), "revolveType" : RevolveType.FULL});
        }
        {
            var Q0;
            Q0=makeQuery(id+"F41.opRevolve","SWEPT_BODY",BODY,{"disambiguationData":[OSD([sQuery(id+"F40.wireOp",EDGE,"E62"),sQuery(id+"F40.wireOp",EDGE,"E63"),sQuery(id+"F40.wireOp",EDGE,"E64"),sQuery(id+"F40.wireOp",EDGE,"E65"),sQuery(id+"F40.wireOp",EDGE,"E66"),sQuery(id+"F40.wireOp",EDGE,"E67"),sQuery(id+"F40.wireOp",EDGE,"Y38QIK3i-MWIf-Q0gZ-pP8j-5flM68i2H9gC"),sQuery(id+"F40.wireOp",EDGE,"E68")])]});
            var Q1;
            Q1=makeQuery(id+"F27.opExtrude","SWEPT_FACE",FACE,{"disambiguationData":[OSD([sQuery(id+"F26.wireOp",EDGE,"E45")])]});
            transform(context, id + "F42", {"entities" : qUnion([Q0]), "transformType" : TransformType.TRANSLATION_DISTANCE, "transformDirection" : qUnion([Q1]), "distance" : 200 * mm, "oppositeDirection" : true, "makeCopy" : false});
        }
        {
            var Q0;
            Q0=makeQuery(id+"F41.opRevolve","SWEPT_EDGE",EDGE,{"disambiguationData":[OSD([sQuery(id+"F40.wireOp",EDGE,"E62"),sQuery(id+"F40.wireOp",EDGE,"E63")])]});
            var Q1;
            Q1=makeQuery(id+"F41.opRevolve","SWEPT_EDGE",EDGE,{"disambiguationData":[OSD([sQuery(id+"F40.wireOp",EDGE,"E67"),sQuery(id+"F40.wireOp",EDGE,"Y38QIK3i-MWIf-Q0gZ-pP8j-5flM68i2H9gC")])]});
            fillet(context, id + "F43", {"entities" : qUnion([Q0, Q1]), "radius" : 1 * mm, "tangentPropagation" : true, "allowEdgeOverflow" : false});
        }
        {
            var Q0;
            Q0=makeQuery(id+"F41.opRevolve","SWEPT_EDGE",EDGE,{"disambiguationData":[OSD([sQuery(id+"F40.wireOp",EDGE,"E65"),sQuery(id+"F40.wireOp",EDGE,"E66")])]});
            var Q1;
            Q1=makeQuery(id+"F41.opRevolve","SWEPT_EDGE",EDGE,{"disambiguationData":[OSD([sQuery(id+"F40.wireOp",EDGE,"E64"),sQuery(id+"F40.wireOp",EDGE,"E65")])]});
            var Q2;
            Q2=makeQuery(id+"F41.opRevolve","SWEPT_EDGE",EDGE,{"disambiguationData":[OSD([sQuery(id+"F40.wireOp",EDGE,"E72"),sQuery(id+"F40.wireOp",EDGE,"E73")])]});
            fillet(context, id + "F44", {"entities" : qUnion([Q0, Q1, Q2]), "radius" : .5 * mm, "tangentPropagation" : true, "allowEdgeOverflow" : false});
        }
        {
            var Q0;
            Q0=makeQuery(id+"F41.opRevolve","SWEPT_BODY",BODY,{"disambiguationData":[OSD([sQuery(id+"F40.wireOp",EDGE,"E62"),sQuery(id+"F40.wireOp",EDGE,"E63"),sQuery(id+"F40.wireOp",EDGE,"E64"),sQuery(id+"F40.wireOp",EDGE,"E65"),sQuery(id+"F40.wireOp",EDGE,"E66"),sQuery(id+"F40.wireOp",EDGE,"E67"),sQuery(id+"F40.wireOp",EDGE,"Y38QIK3i-MWIf-Q0gZ-pP8j-5flM68i2H9gC"),sQuery(id+"F40.wireOp",EDGE,"E68")])]});
            transform(context, id + "F45", {"entities" : qUnion([Q0]), "transformType" : TransformType.TRANSLATION_3D, "dx" : 10 * mm, "dy" : 0 * mm, "dz" : 0 * mm, "makeCopy" : false});
        }
        {
            var Q0;
            Q0=makeQuery(id+"F41.opRevolve","SWEPT_BODY",BODY,{"disambiguationData":[OSD([sQuery(id+"F40.wireOp",EDGE,"E62"),sQuery(id+"F40.wireOp",EDGE,"E63"),sQuery(id+"F40.wireOp",EDGE,"E64"),sQuery(id+"F40.wireOp",EDGE,"E65"),sQuery(id+"F40.wireOp",EDGE,"E66"),sQuery(id+"F40.wireOp",EDGE,"E67"),sQuery(id+"F40.wireOp",EDGE,"Y38QIK3i-MWIf-Q0gZ-pP8j-5flM68i2H9gC"),sQuery(id+"F40.wireOp",EDGE,"E68")])]});
            var Q1;
            Q1=makeQuery(id+"F27.opExtrude","SWEPT_FACE",FACE,{"disambiguationData":[OSD([sQuery(id+"F26.wireOp",EDGE,"E45")])]});
            circularPattern(context, id + "F46", {"entities" : qUnion([Q0]), "axis" : qUnion([Q1]), "angle" : 360 * degree, "instanceCount" : 3, "equalSpace" : true});
        }
        {
            var Q0;
            Q0=qSketchRegion(id+"F40",true);
            var Q1;
            Q1=makeQuery(id+"F27.opExtrude","SWEPT_FACE",FACE,{"disambiguationData":[OSD([sQuery(id+"F26.wireOp",EDGE,"E45")])]});
            revolve(context, id + "F47", {"entities" : qUnion([Q0]), "axis" : qUnion([Q1]), "revolveType" : RevolveType.FULL});
        }
        {
            var Q0;
            Q0=makeQuery(id+"F47.opRevolve","SWEPT_BODY",BODY,{"disambiguationData":[OSD([sQuery(id+"F40.wireOp",EDGE,"E62"),sQuery(id+"F40.wireOp",EDGE,"E63"),sQuery(id+"F40.wireOp",EDGE,"E64"),sQuery(id+"F40.wireOp",EDGE,"E65"),sQuery(id+"F40.wireOp",EDGE,"E66"),sQuery(id+"F40.wireOp",EDGE,"E67"),sQuery(id+"F40.wireOp",EDGE,"E68"),sQuery(id+"F40.wireOp",EDGE,"E69"),sQuery(id+"F40.wireOp",EDGE,"E70"),sQuery(id+"F40.wireOp",EDGE,"E71"),sQuery(id+"F40.wireOp",EDGE,"E72"),sQuery(id+"F40.wireOp",EDGE,"E73")])]});
            deleteBodies(context, id + "F48", {"entities" : qUnion([Q0])});
        }
        {
            var Q0;
            Q0=qCreatedBy(makeId("Top.planeOp"),FACE);
            var sketch = newSketch(context, id + "F49", { "sketchPlane" : qUnion([Q0])});
            skLineSegment(sketch, "E74", {"start": v(-63, -390) * mm, "end": v(-193, -390) * mm});
            skLineSegment(sketch, "E75", {"start": v(-223, -360) * mm, "end": v(-223, -260) * mm});
            skLineSegment(sketch, "E76", {"start": v(-193, -230) * mm, "end": v(-63, -230) * mm});
            skPoint(sketch, "E77.visualSharp", {"position": v(-223, -390) * mm});
            skArc(sketch, "E77.filletArc", {"start": v(-223, -360) * mm, "mid": v(-217.37, -377.5) * mm, "end": v(-202.58, -388.43) * mm});
            skPoint(sketch, "E78.visualSharp", {"position": v(-223, -230) * mm});
            skArc(sketch, "E78.filletArc", {"start": v(-193, -230) * mm, "mid": v(-209.96, -235.25) * mm, "end": v(-220.98, -249.17) * mm});
            skPoint(sketch, "E79.visualSharp", {"position": v(-193, -390) * mm});
            skArc(sketch, "E79.filletArc", {"start": v(-202.58, -388.43) * mm, "mid": v(-197.85, -389.6) * mm, "end": v(-193, -390) * mm});
            skPoint(sketch, "E80.visualSharp", {"position": v(-223, -260) * mm});
            skArc(sketch, "E80.filletArc", {"start": v(-220.98, -249.17) * mm, "mid": v(-222.5, -254.5) * mm, "end": v(-223, -260) * mm});
            skSolve(sketch);
        }
        {
            var Q0;
            Q0=qCreatedBy(makeId("Right.planeOp"),FACE);
            cPlane(context, id + "F50", {"entities" : qUnion([Q0]), "cplaneType" : CPlaneType.OFFSET, "offset" : 63 * mm, "oppositeDirection" : true, "width" : 150 * mm, "height" : 150 * mm});
        }
        {
            var Q0;
            Q0=qCreatedBy(id+"F50.planeOp",FACE);
            var sketch = newSketch(context, id + "F51", { "sketchPlane" : qUnion([Q0])});
            skCircle(sketch, "E81", {"center": v(-390.01, 0) * mm, "radius": 6.25 * mm});
            skCircle(sketch, "E82", {"center": v(-390.01, 0) * mm, "radius": 5 * mm});
            skSolve(sketch);
        }
        {
            var Q0;
            Q0=qSketchRegion(id+"F51",true);
            var Q1;
            Q1=qConstructionFilter(qBodyType(qCreatedBy(id+"F49",EDGE),BodyType.WIRE),ConstructionObject.NO);
            sweep(context, id + "F52", {"operationType" : NewBodyOperationType.ADD, "profiles" : qUnion([Q0]), "path" : qUnion([Q1])});
        }
        {
            var Q0;
            Q0=qSketchRegion(id+"F51",true);
            var Q1;
            Q1=qConstructionFilter(qBodyType(qCreatedBy(id+"F49",EDGE),BodyType.WIRE),ConstructionObject.NO);
            sweep(context, id + "F53", {"operationType" : NewBodyOperationType.ADD, "profiles" : qUnion([Q0]), "path" : qUnion([Q1])});
        }
        {
            var Q0;
            Q0=makeQuery(id+"F52.boolean.opBoolean","INTERSECT",EDGE,{"derivedFrom":[makeQuery(id+"F22.opExtrude","SWEPT_FACE",FACE,{"disambiguationData":[OSD([sQuery(id+"F21.wireOp",EDGE,"E43")])]}),makeQuery(id+"F52.opSweep","SWEPT_FACE",FACE,{"disambiguationData":[OSD([sQuery(id+"F49.wireOp",EDGE,"E76"),sQuery(id+"F51.wireOp",EDGE,"E81")])]})]});
            var Q1;
            Q1=makeQuery(id+"F52.boolean.opBoolean","INTERSECT",EDGE,{"derivedFrom":[makeQuery(id+"F22.opExtrude","SWEPT_FACE",FACE,{"disambiguationData":[OSD([sQuery(id+"F21.wireOp",EDGE,"E43")])]}),makeQuery(id+"F52.opSweep","SWEPT_FACE",FACE,{"disambiguationData":[OSD([sQuery(id+"F49.wireOp",EDGE,"E74"),sQuery(id+"F51.wireOp",EDGE,"E81")])]})]});
            fillet(context, id + "F54", {"entities" : qUnion([Q0, Q1]), "radius" : 3 * mm, "tangentPropagation" : true, "allowEdgeOverflow" : false});
        }
        {
            var Q0;
            Q0=makeQuery(id+"F27.opExtrude","SWEPT_BODY",BODY,{"disambiguationData":[OSD([sQuery(id+"F26.wireOp",EDGE,"E45"),sQuery(id+"F26.wireOp",EDGE,"E46")])]});
            var Q1;
            Q1=makeQuery(id+"F27.opExtrude","SWEPT_FACE",FACE,{"disambiguationData":[OSD([sQuery(id+"F26.wireOp",EDGE,"E45")])]});
            transform(context, id + "F55", {"entities" : qUnion([Q0]), "transformType" : TransformType.TRANSLATION_DISTANCE, "transformDirection" : qUnion([Q1]), "distance" : 73 * mm, "makeCopy" : false});
        }
        {
            var Q0;
            Q0=makeQuery(id+"F41.opRevolve","SWEPT_BODY",BODY,{"disambiguationData":[OSD([sQuery(id+"F40.wireOp",EDGE,"E62"),sQuery(id+"F40.wireOp",EDGE,"E63"),sQuery(id+"F40.wireOp",EDGE,"E64"),sQuery(id+"F40.wireOp",EDGE,"E65"),sQuery(id+"F40.wireOp",EDGE,"E66"),sQuery(id+"F40.wireOp",EDGE,"E67"),sQuery(id+"F40.wireOp",EDGE,"E68"),sQuery(id+"F40.wireOp",EDGE,"E69"),sQuery(id+"F40.wireOp",EDGE,"E70"),sQuery(id+"F40.wireOp",EDGE,"E71"),sQuery(id+"F40.wireOp",EDGE,"E72"),sQuery(id+"F40.wireOp",EDGE,"E73")])]});
            deleteBodies(context, id + "F56", {"entities" : qUnion([Q0])});
        }
        {
            var Q0;
            Q0=makeQuery(id+"F39.opPattern","COPY",BODY,{"derivedFrom":makeQuery(id+"F9.opRevolve","SWEPT_BODY",BODY,{"disambiguationData":[OSD([sQuery(id+"F8.wireOp",EDGE,"E26")])]}),"instanceName":"1"});
            deleteBodies(context, id + "F57", {"entities" : qUnion([Q0])});
        }
        {
            var Q0;
            Q0=makeQuery(id+"F12.opRevolve","SWEPT_BODY",BODY,{"disambiguationData":[OSD([sQuery(id+"F11.wireOp",EDGE,"E28"),sQuery(id+"F11.wireOp",EDGE,"E29"),sQuery(id+"F11.wireOp",EDGE,"E30"),sQuery(id+"F11.wireOp",EDGE,"E31"),sQuery(id+"F11.wireOp",EDGE,"E32"),sQuery(id+"F11.wireOp",EDGE,"E33"),sQuery(id+"F11.wireOp",EDGE,"E34"),sQuery(id+"F11.wireOp",EDGE,"E35"),sQuery(id+"F11.wireOp",EDGE,"E36"),sQuery(id+"F11.wireOp",EDGE,"E37"),sQuery(id+"F11.wireOp",EDGE,"E38"),sQuery(id+"F11.wireOp",EDGE,"E39")])]});
            var Q1;
            {var subQ0=sQuery(id+"F21.wireOp",EDGE,"E43");Q1=makeQuery(id+"F52.boolean.opBoolean","SPLIT",FACE,{"disambiguationData":[TD([makeQuery(id+"F23.opFillet","BLEND_FACE",FACE,{"disambiguationData":[OSD([subQ0]),TDD([makeQuery(id+"F22.opExtrude","CAP_EDGE",EDGE,{"disambiguationData":[OSD([subQ0])],"isStart":true})])]})])],"derivedFrom":makeQuery(id+"F22.opExtrude","SWEPT_FACE",FACE,{"disambiguationData":[OSD([subQ0])]})});}
            transform(context, id + "F58", {"entities" : qUnion([Q0]), "transformType" : TransformType.TRANSLATION_DISTANCE, "transformDirection" : qUnion([Q1]), "distance" : 65 * mm, "makeCopy" : false});
        }
        {
            var Q0;
            Q0=makeQuery(id+"F22.opExtrude","SWEPT_BODY",BODY,{"disambiguationData":[OSD([sQuery(id+"F21.wireOp",EDGE,"E43"),sQuery(id+"F21.wireOp",EDGE,"E44")])]});
            var Q1;
            {var subQ0=sQuery(id+"F21.wireOp",EDGE,"E43");Q1=makeQuery(id+"F52.boolean.opBoolean","SPLIT",FACE,{"disambiguationData":[TD([makeQuery(id+"F23.opFillet","BLEND_FACE",FACE,{"disambiguationData":[OSD([subQ0]),TDD([makeQuery(id+"F22.opExtrude","CAP_EDGE",EDGE,{"disambiguationData":[OSD([subQ0])],"isStart":true})])]})])],"derivedFrom":makeQuery(id+"F22.opExtrude","SWEPT_FACE",FACE,{"disambiguationData":[OSD([subQ0])]})});}
            transform(context, id + "F59", {"entities" : qUnion([Q0]), "transformType" : TransformType.TRANSLATION_DISTANCE, "transformDirection" : qUnion([Q1]), "distance" : 330 * mm, "makeCopy" : false});
        }
    });
